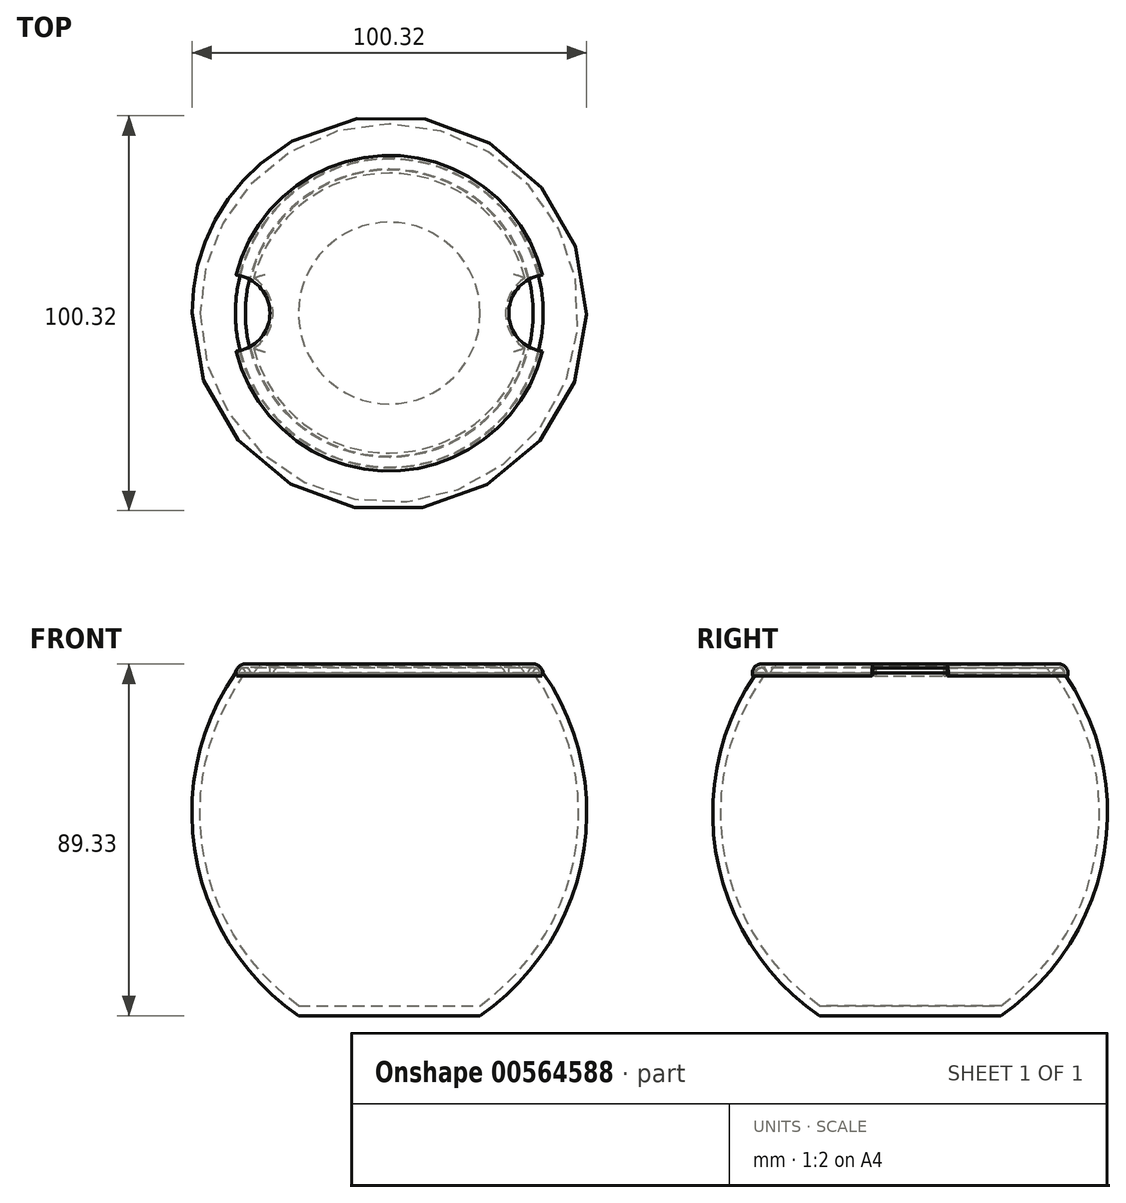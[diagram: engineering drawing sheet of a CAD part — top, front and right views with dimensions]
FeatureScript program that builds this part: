
annotation { "Feature Type Name" : "Feature", "Feature Type Description" : "" }
export const myFeature = defineFeature(function(context is Context, id is Id, definition is map)
    precondition{}
    {
        {
            var Q0;
            Q0=qCreatedBy(makeId("Front.planeOp"),FACE);
            var sketch = newSketch(context, id + "F0", { "sketchPlane" : qUnion([Q0])});
            skCircle(sketch, "E0", {"center": v(-37.83, 0) * mm, "radius": 1.27 * mm});
            skLineSegment(sketch, "E1", {"start": v(-39.1, 0) * mm, "end": v(0, 0) * mm, "construction": true});
            skCircle(sketch, "E2", {"center": v(-37.83, 0) * mm, "radius": 1.47 * mm});
            skLineSegment(sketch, "E3", {"start": v(-36.9, 2.07) * mm, "end": v(0, 2.07) * mm});
            skLineSegment(sketch, "E4", {"start": v(0, 2.07) * mm, "end": v(0, 2.27) * mm});
            skLineSegment(sketch, "E5", {"start": v(0, 2.27) * mm, "end": v(-37.83, 2.27) * mm});
            skCircle(sketch, "E6", {"center": v(-37.83, 0) * mm, "radius": 2.27 * mm});
            skLineSegment(sketch, "E7", {"start": v(-37.83, 0) * mm, "end": v(-35.86, -1.14) * mm, "construction": true});
            skLineSegment(sketch, "E8", {"start": v(-37.83, 0) * mm, "end": v(-39.8, -1.13) * mm, "construction": true});
            skPoint(sketch, "E9", {"position": v(-36.36, 0) * mm});
            skLineSegment(sketch, "E10", {"start": v(-36.36, 0) * mm, "end": v(-35.56, 0) * mm});
            skLineSegment(sketch, "E11", {"start": v(-39.3, 0) * mm, "end": v(-40.1, 0) * mm});
            skLineSegment(sketch, "E12", {"start": v(-35.56, 0) * mm, "end": v(-35.56, 2.07) * mm});
            skLineSegment(sketch, "E13", {"start": v(-39.1, -0.73) * mm, "end": v(-39.98, -0.73) * mm});
            skLineSegment(sketch, "E14", {"start": v(-36.56, -0.74) * mm, "end": v(-35.68, -0.74) * mm});
            skLineSegment(sketch, "E15", {"start": v(-35.56, 0) * mm, "end": v(-35.56, -0.74) * mm});
            skLineSegment(sketch, "E16", {"start": v(-35.56, -0.74) * mm, "end": v(-35.68, -0.74) * mm});
            skSolve(sketch);
        }
        {
            var Q0;
            {var subQ4=sQuery(id+"F0.wireOp",EDGE,"E10");Q0=makeQuery(id+"F0.imprint","IMPRINT",FACE,{"disambiguationData":[TD([[makeQuery(id+"F0.imprint","IMPRINT",EDGE,{"derivedFrom":subQ4}),1.0]])]});}
            var Q1;
            {var subQ0=sQuery(id+"F0.wireOp",EDGE,"E3");Q1=makeQuery(id+"F0.imprint","IMPRINT",FACE,{"disambiguationData":[TD([[makeQuery(id+"F0.imprint","IMPRINT",EDGE,{"derivedFrom":subQ0}),1.0]])]});}
            var Q2;
            {var subQ3=sQuery(id+"F0.wireOp",EDGE,"E12");Q2=makeQuery(id+"F0.imprint","IMPRINT",FACE,{"disambiguationData":[TD([[makeQuery(id+"F0.imprint","IMPRINT",EDGE,{"derivedFrom":subQ3}),1.0]])]});}
            var Q3;
            {var subQ0=sQuery(id+"F0.wireOp",EDGE,"E11");Q3=makeQuery(id+"F0.imprint","IMPRINT",FACE,{"disambiguationData":[TD([[makeQuery(id+"F0.imprint","IMPRINT",EDGE,{"derivedFrom":subQ0}),1.0]])]});}
            var Q4;
            {var subQ0=sQuery(id+"F0.wireOp",EDGE,"E10");Q4=makeQuery(id+"F0.imprint","IMPRINT",FACE,{"disambiguationData":[TD([[makeQuery(id+"F0.imprint","IMPRINT",EDGE,{"derivedFrom":subQ0}),-1.0]])]});}
            var Q5;
            {var subQ0=sQuery(id+"F0.wireOp",EDGE,"E15");Q5=makeQuery(id+"F0.imprint","IMPRINT",FACE,{"disambiguationData":[TD([[makeQuery(id+"F0.imprint","IMPRINT",EDGE,{"derivedFrom":subQ0}),-1.0]])]});}
            var Q6;
            Q6=sQuery(id+"F0.wireOp",EDGE,"E4");
            revolve(context, id + "F1", {"entities" : qUnion([Q0, Q1, Q2, Q3, Q4, Q5]), "axis" : qUnion([Q6]), "revolveType" : RevolveType.FULL});
        }
        {
            var Q0;
            Q0=makeQuery(id+"F1.opRevolve","SWEPT_FACE",FACE,{"disambiguationData":[OSD([sQuery(id+"F0.wireOp",EDGE,"E5")])]});
            var sketch = newSketch(context, id + "F2", { "sketchPlane" : qUnion([Q0])});
            skCircle(sketch, "E17", {"center": v(40.1, 0) * mm, "radius": 9.75 * mm});
            skCircle(sketch, "E18", {"center": v(-40.1, 0) * mm, "radius": 9.75 * mm});
            skCircle(sketch, "E19", {"center": v(40.1, 0) * mm, "radius": 10.55 * mm});
            skCircle(sketch, "E20", {"center": v(-40.1, 0) * mm, "radius": 10.55 * mm});
            skCircle(sketch, "E21", {"center": v(0, 0) * mm, "radius": 36.36 * mm});
            skLineSegment(sketch, "E22", {"start": v(0, 0) * mm, "end": v(0, -36.36) * mm, "construction": true});
            skLineSegment(sketch, "E23", {"start": v(0, 0) * mm, "end": v(-40.1, 0) * mm, "construction": true});
            skLineSegment(sketch, "E24", {"start": v(0, 0) * mm, "end": v(40.1, 0) * mm, "construction": true});
            skSolve(sketch);
        }
        {
            var Q0;
            {var subQ0=sQuery(id+"F2.wireOp",EDGE,"E17");var subQ1=makeQuery(id+"F1.opRevolve","SWEPT_EDGE",EDGE,{"disambiguationData":[OSD([sQuery(id+"F0.wireOp",EDGE,"E5"),sQuery(id+"F0.wireOp",EDGE,"E6")])]});var subQ2=makeQuery(id+"F2.imprint","INTERSECT",VERTEX,{"disambiguationData":[OD(0.0)],"derivedFrom":[subQ1,subQ0]});Q0=makeQuery(id+"F2.imprint","IMPRINT",FACE,{"disambiguationData":[TD([[makeQuery(id+"F2.imprint","IMPRINT",EDGE,{"disambiguationData":[TD([[subQ2,1.0]])],"derivedFrom":subQ0}),1.0]])]});}
            var Q1;
            {var subQ0=sQuery(id+"F2.wireOp",EDGE,"E17");var subQ1=makeQuery(id+"F1.opRevolve","SWEPT_EDGE",EDGE,{"disambiguationData":[OSD([sQuery(id+"F0.wireOp",EDGE,"E5"),sQuery(id+"F0.wireOp",EDGE,"E6")])]});var subQ2=makeQuery(id+"F2.imprint","INTERSECT",VERTEX,{"disambiguationData":[OD(0.0)],"derivedFrom":[subQ1,subQ0]});Q1=makeQuery(id+"F2.imprint","IMPRINT",FACE,{"disambiguationData":[TD([[makeQuery(id+"F2.imprint","IMPRINT",EDGE,{"disambiguationData":[TD([[subQ2,-1.0]])],"derivedFrom":subQ0}),1.0]])]});}
            var Q2;
            {var subQ0=sQuery(id+"F2.wireOp",EDGE,"E18");var subQ1=makeQuery(id+"F1.opRevolve","SWEPT_EDGE",EDGE,{"disambiguationData":[OSD([sQuery(id+"F0.wireOp",EDGE,"E5"),sQuery(id+"F0.wireOp",EDGE,"E6")])]});var subQ2=makeQuery(id+"F2.imprint","INTERSECT",VERTEX,{"disambiguationData":[OD(0.0)],"derivedFrom":[subQ1,subQ0]});Q2=makeQuery(id+"F2.imprint","IMPRINT",FACE,{"disambiguationData":[TD([[makeQuery(id+"F2.imprint","IMPRINT",EDGE,{"disambiguationData":[TD([[subQ2,1.0]])],"derivedFrom":subQ0}),1.0]])]});}
            var Q3;
            {var subQ0=sQuery(id+"F2.wireOp",EDGE,"E18");var subQ1=makeQuery(id+"F1.opRevolve","SWEPT_EDGE",EDGE,{"disambiguationData":[OSD([sQuery(id+"F0.wireOp",EDGE,"E5"),sQuery(id+"F0.wireOp",EDGE,"E6")])]});var subQ2=makeQuery(id+"F2.imprint","INTERSECT",VERTEX,{"disambiguationData":[OD(0.0)],"derivedFrom":[subQ1,subQ0]});Q3=makeQuery(id+"F2.imprint","IMPRINT",FACE,{"disambiguationData":[TD([[makeQuery(id+"F2.imprint","IMPRINT",EDGE,{"disambiguationData":[TD([[subQ2,-1.0]])],"derivedFrom":subQ0}),1.0]])]});}
            var Q4;
            {var subQ0=sQuery(id+"F2.wireOp",EDGE,"E21");var subQ1=sQuery(id+"F2.wireOp",EDGE,"E17");var subQ2=makeQuery(id+"F2.imprint","INTERSECT",VERTEX,{"disambiguationData":[OD(0.0)],"derivedFrom":[subQ1,subQ0]});Q4=makeQuery(id+"F2.imprint","IMPRINT",FACE,{"disambiguationData":[TD([[makeQuery(id+"F2.imprint","IMPRINT",EDGE,{"disambiguationData":[TD([[subQ2,-1.0]])],"derivedFrom":subQ1}),1.0]])]});}
            var Q5;
            {var subQ0=sQuery(id+"F2.wireOp",EDGE,"E21");var subQ1=sQuery(id+"F2.wireOp",EDGE,"E18");var subQ2=makeQuery(id+"F2.imprint","INTERSECT",VERTEX,{"disambiguationData":[OD(0.0)],"derivedFrom":[subQ1,subQ0]});Q5=makeQuery(id+"F2.imprint","IMPRINT",FACE,{"disambiguationData":[TD([[makeQuery(id+"F2.imprint","IMPRINT",EDGE,{"disambiguationData":[TD([[subQ2,1.0]])],"derivedFrom":subQ1}),1.0]])]});}
            extrude(context, id + "F3", {"entities" : qUnion([Q0, Q1, Q2, Q3, Q4, Q5]), "operationType" : NewBodyOperationType.REMOVE, "oppositeDirection" : true, "depth" : 25 * mm, "offsetDistance" : 25 * mm});
        }
        {
            var Q0;
            {var subQ0=sQuery(id+"F2.wireOp",EDGE,"E21");var subQ1=sQuery(id+"F2.wireOp",EDGE,"E17");var subQ2=makeQuery(id+"F2.imprint","INTERSECT",VERTEX,{"disambiguationData":[OD(0.0)],"derivedFrom":[subQ1,subQ0]});Q0=makeQuery(id+"F2.imprint","IMPRINT",FACE,{"disambiguationData":[TD([[makeQuery(id+"F2.imprint","IMPRINT",EDGE,{"disambiguationData":[TD([[subQ2,-1.0]])],"derivedFrom":subQ1}),-1.0]])]});}
            var Q1;
            {var subQ0=sQuery(id+"F2.wireOp",EDGE,"E21");var subQ1=sQuery(id+"F2.wireOp",EDGE,"E18");var subQ2=makeQuery(id+"F2.imprint","INTERSECT",VERTEX,{"disambiguationData":[OD(0.0)],"derivedFrom":[subQ1,subQ0]});Q1=makeQuery(id+"F2.imprint","IMPRINT",FACE,{"disambiguationData":[TD([[makeQuery(id+"F2.imprint","IMPRINT",EDGE,{"disambiguationData":[TD([[subQ2,1.0]])],"derivedFrom":subQ1}),-1.0]])]});}
            var Q2;
            Q2=makeQuery(id+"F3.boolean.opBoolean","SPLIT",FACE,{"disambiguationData":[OD(1.0)],"derivedFrom":makeQuery(id+"F1.opRevolve","SWEPT_FACE",FACE,{"disambiguationData":[OSD([sQuery(id+"F0.wireOp",EDGE,"E14")])]})});
            extrude(context, id + "F4", {"entities" : qUnion([Q0, Q1]), "operationType" : NewBodyOperationType.ADD, "endBound" : BoundingType.UP_TO_SURFACE, "oppositeDirection" : true, "depth" : 25 * mm, "endBoundEntityFace" : qUnion([Q2]), "offsetDistance" : 25 * mm});
        }
        {
            var Q0;
            Q0=makeQuery(id+"F1.opRevolve","SWEPT_FACE",FACE,{"disambiguationData":[OSD([sQuery(id+"F0.wireOp",EDGE,"E3")])]});
            fillet(context, id + "F5", {"entities" : qUnion([Q0]), "radius" : 2.8 * mm, "tangentPropagation" : true, "allowEdgeOverflow" : false});
        }
        {
            var Q0;
            Q0=qCreatedBy(makeId("Front.planeOp"),FACE);
            var sketch = newSketch(context, id + "F6", { "sketchPlane" : qUnion([Q0])});
            skArc(sketch, "E25", {"start": v(-36.56, 0) * mm, "mid": v(-47.33, -45.05) * mm, "end": v(-23.1, -84.52) * mm});
            skArc(sketch, "E26", {"start": v(-39.1, 0) * mm, "mid": v(-49.13, -46.84) * mm, "end": v(-23.1, -87.06) * mm});
            skLineSegment(sketch, "E27", {"start": v(-23.1, -87.06) * mm, "end": v(-23.1, -84.52) * mm, "construction": true});
            skLineSegment(sketch, "E28", {"start": v(-36.56, 0) * mm, "end": v(-39.1, 0) * mm, "construction": true});
            skLineSegment(sketch, "E29", {"start": v(-23.1, -84.52) * mm, "end": v(0, -84.52) * mm});
            skLineSegment(sketch, "E30", {"start": v(0, -84.52) * mm, "end": v(0, -87.06) * mm});
            skLineSegment(sketch, "E31", {"start": v(0, -87.06) * mm, "end": v(-23.1, -87.06) * mm});
            skArc(sketch, "E32", {"start": v(-36.56, 0) * mm, "mid": v(-37.83, 1.27) * mm, "end": v(-39.1, 0) * mm});
            skArc(sketch, "E33", {"start": v(-39.1, 0) * mm, "mid": v(-37.83, -1.27) * mm, "end": v(-36.56, 0) * mm, "construction": true});
            skSolve(sketch);
        }
        {
            var Q0;
            Q0=makeQuery(id+"F6.imprint","IMPRINT",FACE,{"disambiguationData":[TD([[makeQuery(id+"F6.imprint","IMPRINT",EDGE,{"derivedFrom":sQuery(id+"F6.wireOp",EDGE,"E25")}),-1.0]])]});
            var Q1;
            Q1=sQuery(id+"F0.wireOp",EDGE,"E4");
            revolve(context, id + "F7", {"entities" : qUnion([Q0]), "axis" : qUnion([Q1]), "revolveType" : RevolveType.FULL});
        }
    });
